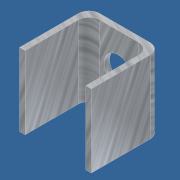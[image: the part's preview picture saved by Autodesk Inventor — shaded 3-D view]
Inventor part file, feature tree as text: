
AUTODESK INVENTOR PART (.ipt)
format: ipt  version: 2012 (Build 160160000, 160)  size: 133,632 bytes
history: native  units: in
note: dims shown in document units (in); Inventor stores cm internally (conversion verified against a paired STEP export)
features: sketch x4, extrude x2, fillet x2, hole x1
ambient origin geometry x8: Origin, YZ Plane, XZ Plane, XY Plane, X Axis, Y Axis, Z Axis, Center Point
bodies: Solid1 (feature_tree)
feature tree (9):
  extrude  "Extrusion1"  Depth=0.34in
  extrude  "Extrusion2"  Depth=0.026in
  fillet  "Fillet1"  Radius=0.026in
  fillet  "Fillet2"  Radius=0.298in
  hole  "Hole1"  [1 undecoded]
  sketch  "Sketch4"  dims[d10=0.131in d11=0.5in d12=0.375in d13=0.25in d14=0.5635in d15=0.75in d16=0.8108in]
  sketch  "Sketch1"  dims[d0=0.335in d1=0.34in]
  sketch  "Sketch2"  dims[d2=0.026in d3=0.0in d4=0.026in d5=0.026in d6=0.298in d7=0.0in]
  sketch  "Sketch3"  dims[d8=0.05in d9=0.05in]
note: 1 required parameter value undecoded (feature->parameter linkage not recoverable at this tier; creation-order binding heuristic only, values carry confidence <= 0.55)
